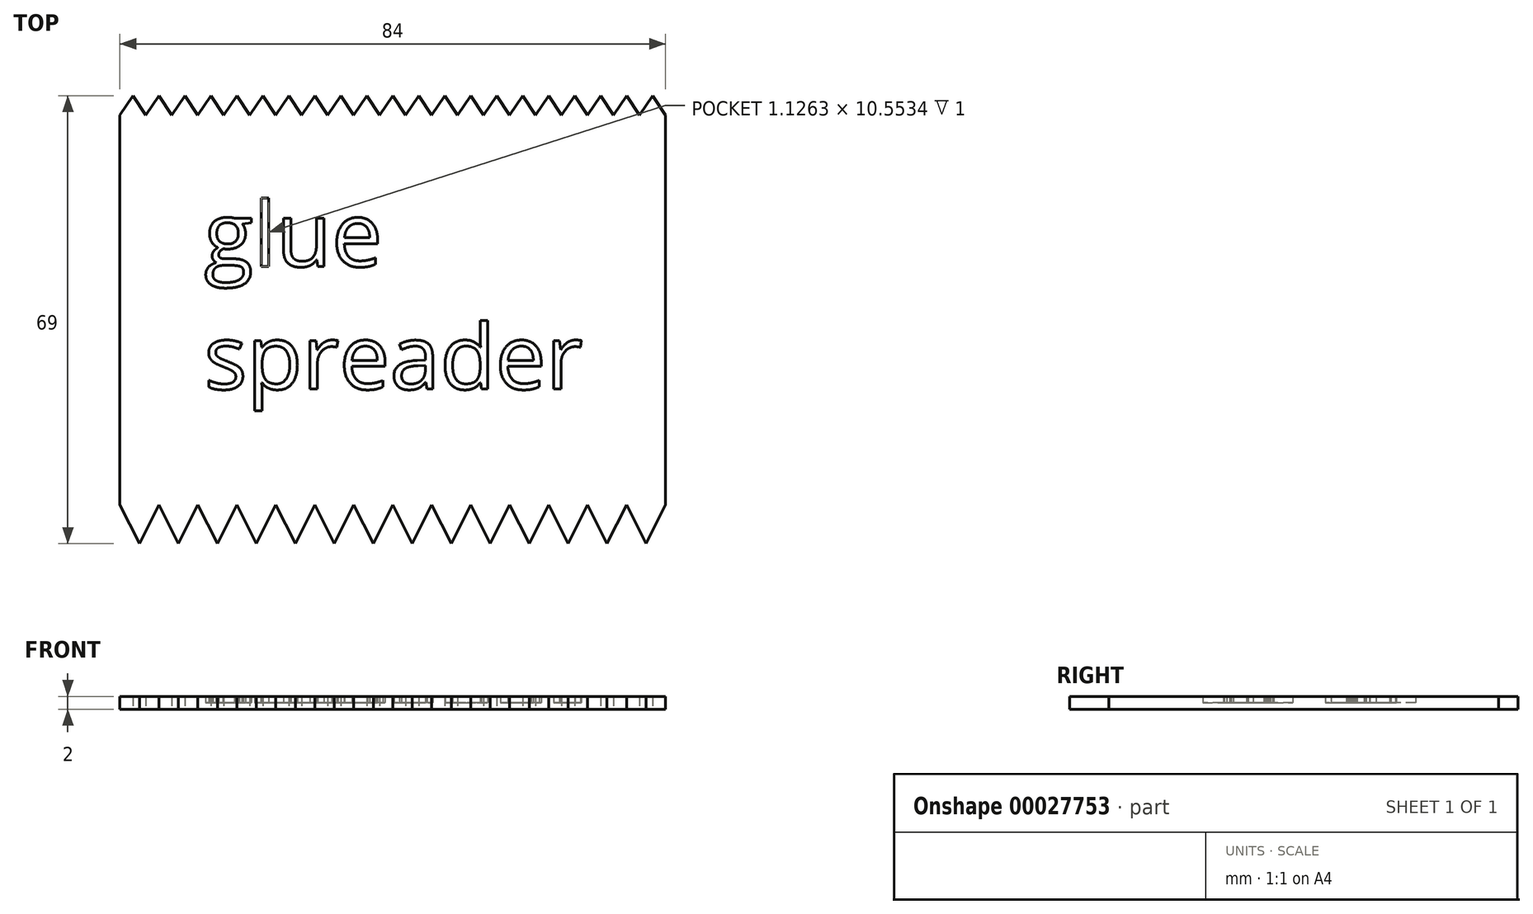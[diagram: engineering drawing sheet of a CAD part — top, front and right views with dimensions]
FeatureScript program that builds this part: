
annotation { "Feature Type Name" : "Feature", "Feature Type Description" : "" }
export const myFeature = defineFeature(function(context is Context, id is Id, definition is map)
    precondition{}
    {
        {
            var Q0;
            Q0=qCreatedBy(makeId("Top.planeOp"),FACE);
            var sketch = newSketch(context, id + "F0", { "sketchPlane" : qUnion([Q0])});
            skLineSegment(sketch, "E0.rect.bottom", {"start": v(42, 30) * mm, "end": v(-42, 30) * mm});
            skLineSegment(sketch, "E0.rect.top", {"start": v(42, -30) * mm, "end": v(-42, -30) * mm});
            skLineSegment(sketch, "E0.rect.left", {"start": v(42, 30) * mm, "end": v(42, -30) * mm});
            skLineSegment(sketch, "E0.rect.right", {"start": v(-42, 30) * mm, "end": v(-42, -30) * mm});
            skPoint(sketch, "E0.rect.middle", {"position": v(0, 0) * mm});
            skLineSegment(sketch, "E1", {"start": v(-42, 30) * mm, "end": v(-40, 33) * mm});
            skLineSegment(sketch, "E2", {"start": v(-40, 33) * mm, "end": v(-38, 30) * mm});
            skLineSegment(sketch, "E3.1.0.0", {"start": v(-38, 30) * mm, "end": v(-36, 33) * mm});
            skLineSegment(sketch, "E3.1.0.1", {"start": v(-36, 33) * mm, "end": v(-34, 30) * mm});
            skLineSegment(sketch, "E3.2.0.0", {"start": v(-34, 30) * mm, "end": v(-32, 33) * mm});
            skLineSegment(sketch, "E3.2.0.1", {"start": v(-32, 33) * mm, "end": v(-30, 30) * mm});
            skLineSegment(sketch, "E3.3.0.0", {"start": v(-30, 30) * mm, "end": v(-28, 33) * mm});
            skLineSegment(sketch, "E3.3.0.1", {"start": v(-28, 33) * mm, "end": v(-26, 30) * mm});
            skLineSegment(sketch, "E3.4.0.0", {"start": v(-26, 30) * mm, "end": v(-24, 33) * mm});
            skLineSegment(sketch, "E3.4.0.1", {"start": v(-24, 33) * mm, "end": v(-22, 30) * mm});
            skLineSegment(sketch, "E3.5.0.0", {"start": v(-22, 30) * mm, "end": v(-20, 33) * mm});
            skLineSegment(sketch, "E3.5.0.1", {"start": v(-20, 33) * mm, "end": v(-18, 30) * mm});
            skLineSegment(sketch, "E3.6.0.0", {"start": v(-18, 30) * mm, "end": v(-16, 33) * mm});
            skLineSegment(sketch, "E3.6.0.1", {"start": v(-16, 33) * mm, "end": v(-14, 30) * mm});
            skLineSegment(sketch, "E3.7.0.0", {"start": v(-14, 30) * mm, "end": v(-12, 33) * mm});
            skLineSegment(sketch, "E3.7.0.1", {"start": v(-12, 33) * mm, "end": v(-10, 30) * mm});
            skLineSegment(sketch, "E3.8.0.0", {"start": v(-10, 30) * mm, "end": v(-8, 33) * mm});
            skLineSegment(sketch, "E3.8.0.1", {"start": v(-8, 33) * mm, "end": v(-6, 30) * mm});
            skLineSegment(sketch, "E3.9.0.0", {"start": v(-6, 30) * mm, "end": v(-4, 33) * mm});
            skLineSegment(sketch, "E3.9.0.1", {"start": v(-4, 33) * mm, "end": v(-2, 30) * mm});
            skLineSegment(sketch, "E3.10.0.0", {"start": v(-2, 30) * mm, "end": v(0, 33) * mm});
            skLineSegment(sketch, "E3.10.0.1", {"start": v(0, 33) * mm, "end": v(2, 30) * mm});
            skLineSegment(sketch, "E3.11.0.0", {"start": v(2, 30) * mm, "end": v(4, 33) * mm});
            skLineSegment(sketch, "E3.11.0.1", {"start": v(4, 33) * mm, "end": v(6, 30) * mm});
            skLineSegment(sketch, "E3.12.0.0", {"start": v(6, 30) * mm, "end": v(8, 33) * mm});
            skLineSegment(sketch, "E3.12.0.1", {"start": v(8, 33) * mm, "end": v(10, 30) * mm});
            skLineSegment(sketch, "E3.13.0.0", {"start": v(10, 30) * mm, "end": v(12, 33) * mm});
            skLineSegment(sketch, "E3.13.0.1", {"start": v(12, 33) * mm, "end": v(14, 30) * mm});
            skLineSegment(sketch, "E3.14.0.0", {"start": v(14, 30) * mm, "end": v(16, 33) * mm});
            skLineSegment(sketch, "E3.14.0.1", {"start": v(16, 33) * mm, "end": v(18, 30) * mm});
            skLineSegment(sketch, "E3.direction1", {"start": v(-42, 30) * mm, "end": v(-38, 30) * mm, "construction": true});
            skLineSegment(sketch, "E4", {"start": v(-42, -30) * mm, "end": v(-39, -36) * mm});
            skLineSegment(sketch, "E5", {"start": v(-39, -36) * mm, "end": v(-36, -30) * mm});
            skLineSegment(sketch, "E6.1.0.0", {"start": v(-33, -36) * mm, "end": v(-30, -30) * mm});
            skLineSegment(sketch, "E6.1.0.1", {"start": v(-36, -30) * mm, "end": v(-33, -36) * mm});
            skLineSegment(sketch, "E6.2.0.0", {"start": v(-27, -36) * mm, "end": v(-24, -30) * mm});
            skLineSegment(sketch, "E6.2.0.1", {"start": v(-30, -30) * mm, "end": v(-27, -36) * mm});
            skLineSegment(sketch, "E6.3.0.0", {"start": v(-21, -36) * mm, "end": v(-18, -30) * mm});
            skLineSegment(sketch, "E6.3.0.1", {"start": v(-24, -30) * mm, "end": v(-21, -36) * mm});
            skLineSegment(sketch, "E6.4.0.0", {"start": v(-15, -36) * mm, "end": v(-12, -30) * mm});
            skLineSegment(sketch, "E6.4.0.1", {"start": v(-18, -30) * mm, "end": v(-15, -36) * mm});
            skLineSegment(sketch, "E6.5.0.0", {"start": v(-9, -36) * mm, "end": v(-6, -30) * mm});
            skLineSegment(sketch, "E6.5.0.1", {"start": v(-12, -30) * mm, "end": v(-9, -36) * mm});
            skLineSegment(sketch, "E6.6.0.0", {"start": v(-3, -36) * mm, "end": v(0, -30) * mm});
            skLineSegment(sketch, "E6.6.0.1", {"start": v(-6, -30) * mm, "end": v(-3, -36) * mm});
            skLineSegment(sketch, "E6.7.0.0", {"start": v(3, -36) * mm, "end": v(6, -30) * mm});
            skLineSegment(sketch, "E6.7.0.1", {"start": v(0, -30) * mm, "end": v(3, -36) * mm});
            skLineSegment(sketch, "E6.8.0.0", {"start": v(9, -36) * mm, "end": v(12, -30) * mm});
            skLineSegment(sketch, "E6.8.0.1", {"start": v(6, -30) * mm, "end": v(9, -36) * mm});
            skLineSegment(sketch, "E6.9.0.0", {"start": v(15, -36) * mm, "end": v(18, -30) * mm});
            skLineSegment(sketch, "E6.9.0.1", {"start": v(12, -30) * mm, "end": v(15, -36) * mm});
            skLineSegment(sketch, "E6.direction1", {"start": v(-39, -36) * mm, "end": v(-33, -36) * mm, "construction": true});
            skLineSegment(sketch, "E7.0.15.0", {"start": v(18, 30) * mm, "end": v(20, 33) * mm});
            skLineSegment(sketch, "E7.3.15.0", {"start": v(20, 33) * mm, "end": v(22, 30) * mm});
            skLineSegment(sketch, "E7.0.16.0", {"start": v(22, 30) * mm, "end": v(24, 33) * mm});
            skLineSegment(sketch, "E7.3.16.0", {"start": v(24, 33) * mm, "end": v(26, 30) * mm});
            skLineSegment(sketch, "E7.0.17.0", {"start": v(26, 30) * mm, "end": v(28, 33) * mm});
            skLineSegment(sketch, "E7.3.17.0", {"start": v(28, 33) * mm, "end": v(30, 30) * mm});
            skLineSegment(sketch, "E7.0.18.0", {"start": v(30, 30) * mm, "end": v(32, 33) * mm});
            skLineSegment(sketch, "E7.3.18.0", {"start": v(32, 33) * mm, "end": v(34, 30) * mm});
            skLineSegment(sketch, "E7.0.19.0", {"start": v(34, 30) * mm, "end": v(36, 33) * mm});
            skLineSegment(sketch, "E7.3.19.0", {"start": v(36, 33) * mm, "end": v(38, 30) * mm});
            skLineSegment(sketch, "E7.0.20.0", {"start": v(38, 30) * mm, "end": v(40, 33) * mm});
            skLineSegment(sketch, "E7.3.20.0", {"start": v(40, 33) * mm, "end": v(42, 30) * mm});
            skLineSegment(sketch, "E8.0.10.0", {"start": v(21, -36) * mm, "end": v(24, -30) * mm});
            skLineSegment(sketch, "E8.3.10.0", {"start": v(18, -30) * mm, "end": v(21, -36) * mm});
            skLineSegment(sketch, "E8.0.11.0", {"start": v(27, -36) * mm, "end": v(30, -30) * mm});
            skLineSegment(sketch, "E8.3.11.0", {"start": v(24, -30) * mm, "end": v(27, -36) * mm});
            skLineSegment(sketch, "E8.0.12.0", {"start": v(33, -36) * mm, "end": v(36, -30) * mm});
            skLineSegment(sketch, "E8.3.12.0", {"start": v(30, -30) * mm, "end": v(33, -36) * mm});
            skLineSegment(sketch, "E8.0.13.0", {"start": v(39, -36) * mm, "end": v(42, -30) * mm});
            skLineSegment(sketch, "E8.3.13.0", {"start": v(36, -30) * mm, "end": v(39, -36) * mm});
            skText(sketch, "E9", { "text": "glue\nspreader", "fontName": "OpenSans-Regular.ttf"});
            skLineSegment(sketch, "E10", {"start": v(0, 30) * mm, "end": v(0, -30) * mm, "construction": true});
            skLineSegment(sketch, "E11", {"start": v(-42, 0) * mm, "end": v(42, 0) * mm, "construction": true});
            const initialGuessF0  = {"E9": [-0.02905, 0.0067, 1, 0, 0.01]};
            skSetInitialGuess(sketch, initialGuessF0);
            skSolve(sketch);
        }
        {
            var Q0;
            {var subQ1=sQuery(id+"F0.wireOp",EDGE,"E7.0.18.0");Q0=makeQuery(id+"F0.imprint","IMPRINT",FACE,{"disambiguationData":[TD([[makeQuery(id+"F0.imprint","IMPRINT",EDGE,{"derivedFrom":subQ1}),-1.0]])]});}
            var Q1;
            {var subQ1=sQuery(id+"F0.wireOp",EDGE,"E3.8.0.0");Q1=makeQuery(id+"F0.imprint","IMPRINT",FACE,{"disambiguationData":[TD([[makeQuery(id+"F0.imprint","IMPRINT",EDGE,{"derivedFrom":subQ1}),-1.0]])]});}
            var Q2;
            {var subQ1=sQuery(id+"F0.wireOp",EDGE,"E3.10.0.0");Q2=makeQuery(id+"F0.imprint","IMPRINT",FACE,{"disambiguationData":[TD([[makeQuery(id+"F0.imprint","IMPRINT",EDGE,{"derivedFrom":subQ1}),-1.0]])]});}
            var Q3;
            {var subQ1=sQuery(id+"F0.wireOp",EDGE,"E7.0.19.0");Q3=makeQuery(id+"F0.imprint","IMPRINT",FACE,{"disambiguationData":[TD([[makeQuery(id+"F0.imprint","IMPRINT",EDGE,{"derivedFrom":subQ1}),-1.0]])]});}
            var Q4;
            {var subQ1=sQuery(id+"F0.wireOp",EDGE,"E3.13.0.0");Q4=makeQuery(id+"F0.imprint","IMPRINT",FACE,{"disambiguationData":[TD([[makeQuery(id+"F0.imprint","IMPRINT",EDGE,{"derivedFrom":subQ1}),-1.0]])]});}
            var Q5;
            {var subQ1=sQuery(id+"F0.wireOp",EDGE,"E7.0.17.0");Q5=makeQuery(id+"F0.imprint","IMPRINT",FACE,{"disambiguationData":[TD([[makeQuery(id+"F0.imprint","IMPRINT",EDGE,{"derivedFrom":subQ1}),-1.0]])]});}
            var Q6;
            {var subQ1=sQuery(id+"F0.wireOp",EDGE,"E7.0.16.0");Q6=makeQuery(id+"F0.imprint","IMPRINT",FACE,{"disambiguationData":[TD([[makeQuery(id+"F0.imprint","IMPRINT",EDGE,{"derivedFrom":subQ1}),-1.0]])]});}
            var Q7;
            {var subQ1=sQuery(id+"F0.wireOp",EDGE,"E7.0.15.0");Q7=makeQuery(id+"F0.imprint","IMPRINT",FACE,{"disambiguationData":[TD([[makeQuery(id+"F0.imprint","IMPRINT",EDGE,{"derivedFrom":subQ1}),-1.0]])]});}
            var Q8;
            {var subQ1=sQuery(id+"F0.wireOp",EDGE,"E6.6.0.0");Q8=makeQuery(id+"F0.imprint","IMPRINT",FACE,{"disambiguationData":[TD([[makeQuery(id+"F0.imprint","IMPRINT",EDGE,{"derivedFrom":subQ1}),1.0]])]});}
            var Q9;
            {var subQ1=sQuery(id+"F0.wireOp",EDGE,"E8.0.13.0");Q9=makeQuery(id+"F0.imprint","IMPRINT",FACE,{"disambiguationData":[TD([[makeQuery(id+"F0.imprint","IMPRINT",EDGE,{"derivedFrom":subQ1}),1.0]])]});}
            var Q10;
            {var subQ1=sQuery(id+"F0.wireOp",EDGE,"E6.4.0.0");Q10=makeQuery(id+"F0.imprint","IMPRINT",FACE,{"disambiguationData":[TD([[makeQuery(id+"F0.imprint","IMPRINT",EDGE,{"derivedFrom":subQ1}),1.0]])]});}
            var Q11;
            {var subQ1=sQuery(id+"F0.wireOp",EDGE,"E6.5.0.0");Q11=makeQuery(id+"F0.imprint","IMPRINT",FACE,{"disambiguationData":[TD([[makeQuery(id+"F0.imprint","IMPRINT",EDGE,{"derivedFrom":subQ1}),1.0]])]});}
            var Q12;
            {var subQ1=sQuery(id+"F0.wireOp",EDGE,"E8.0.11.0");Q12=makeQuery(id+"F0.imprint","IMPRINT",FACE,{"disambiguationData":[TD([[makeQuery(id+"F0.imprint","IMPRINT",EDGE,{"derivedFrom":subQ1}),1.0]])]});}
            var Q13;
            {var subQ1=sQuery(id+"F0.wireOp",EDGE,"E3.3.0.0");Q13=makeQuery(id+"F0.imprint","IMPRINT",FACE,{"disambiguationData":[TD([[makeQuery(id+"F0.imprint","IMPRINT",EDGE,{"derivedFrom":subQ1}),-1.0]])]});}
            var Q14;
            {var subQ1=sQuery(id+"F0.wireOp",EDGE,"E6.1.0.0");Q14=makeQuery(id+"F0.imprint","IMPRINT",FACE,{"disambiguationData":[TD([[makeQuery(id+"F0.imprint","IMPRINT",EDGE,{"derivedFrom":subQ1}),1.0]])]});}
            var Q15;
            {var subQ1=sQuery(id+"F0.wireOp",EDGE,"E8.0.12.0");Q15=makeQuery(id+"F0.imprint","IMPRINT",FACE,{"disambiguationData":[TD([[makeQuery(id+"F0.imprint","IMPRINT",EDGE,{"derivedFrom":subQ1}),1.0]])]});}
            var Q16;
            {var subQ1=sQuery(id+"F0.wireOp",EDGE,"E3.5.0.0");Q16=makeQuery(id+"F0.imprint","IMPRINT",FACE,{"disambiguationData":[TD([[makeQuery(id+"F0.imprint","IMPRINT",EDGE,{"derivedFrom":subQ1}),-1.0]])]});}
            var Q17;
            {var subQ1=sQuery(id+"F0.wireOp",EDGE,"E3.7.0.0");Q17=makeQuery(id+"F0.imprint","IMPRINT",FACE,{"disambiguationData":[TD([[makeQuery(id+"F0.imprint","IMPRINT",EDGE,{"derivedFrom":subQ1}),-1.0]])]});}
            var Q18;
            {var subQ1=sQuery(id+"F0.wireOp",EDGE,"E6.7.0.0");Q18=makeQuery(id+"F0.imprint","IMPRINT",FACE,{"disambiguationData":[TD([[makeQuery(id+"F0.imprint","IMPRINT",EDGE,{"derivedFrom":subQ1}),1.0]])]});}
            var Q19;
            {var subQ1=sQuery(id+"F0.wireOp",EDGE,"E6.2.0.0");Q19=makeQuery(id+"F0.imprint","IMPRINT",FACE,{"disambiguationData":[TD([[makeQuery(id+"F0.imprint","IMPRINT",EDGE,{"derivedFrom":subQ1}),1.0]])]});}
            var Q20;
            {var subQ1=sQuery(id+"F0.wireOp",EDGE,"E7.0.20.0");Q20=makeQuery(id+"F0.imprint","IMPRINT",FACE,{"disambiguationData":[TD([[makeQuery(id+"F0.imprint","IMPRINT",EDGE,{"derivedFrom":subQ1}),-1.0]])]});}
            var Q21;
            {var subQ1=sQuery(id+"F0.wireOp",EDGE,"E1");Q21=makeQuery(id+"F0.imprint","IMPRINT",FACE,{"disambiguationData":[TD([[makeQuery(id+"F0.imprint","IMPRINT",EDGE,{"derivedFrom":subQ1}),-1.0]])]});}
            var Q22;
            {var subQ1=sQuery(id+"F0.wireOp",EDGE,"E3.9.0.0");Q22=makeQuery(id+"F0.imprint","IMPRINT",FACE,{"disambiguationData":[TD([[makeQuery(id+"F0.imprint","IMPRINT",EDGE,{"derivedFrom":subQ1}),-1.0]])]});}
            var Q23;
            {var subQ1=sQuery(id+"F0.wireOp",EDGE,"E3.11.0.0");Q23=makeQuery(id+"F0.imprint","IMPRINT",FACE,{"disambiguationData":[TD([[makeQuery(id+"F0.imprint","IMPRINT",EDGE,{"derivedFrom":subQ1}),-1.0]])]});}
            var Q24;
            {var subQ1=sQuery(id+"F0.wireOp",EDGE,"E3.12.0.0");Q24=makeQuery(id+"F0.imprint","IMPRINT",FACE,{"disambiguationData":[TD([[makeQuery(id+"F0.imprint","IMPRINT",EDGE,{"derivedFrom":subQ1}),-1.0]])]});}
            var Q25;
            {var subQ1=sQuery(id+"F0.wireOp",EDGE,"E3.6.0.0");Q25=makeQuery(id+"F0.imprint","IMPRINT",FACE,{"disambiguationData":[TD([[makeQuery(id+"F0.imprint","IMPRINT",EDGE,{"derivedFrom":subQ1}),-1.0]])]});}
            var Q26;
            {var subQ1=sQuery(id+"F0.wireOp",EDGE,"E8.0.10.0");Q26=makeQuery(id+"F0.imprint","IMPRINT",FACE,{"disambiguationData":[TD([[makeQuery(id+"F0.imprint","IMPRINT",EDGE,{"derivedFrom":subQ1}),1.0]])]});}
            var Q27;
            {var subQ1=sQuery(id+"F0.wireOp",EDGE,"E3.4.0.0");Q27=makeQuery(id+"F0.imprint","IMPRINT",FACE,{"disambiguationData":[TD([[makeQuery(id+"F0.imprint","IMPRINT",EDGE,{"derivedFrom":subQ1}),-1.0]])]});}
            var Q28;
            {var subQ1=sQuery(id+"F0.wireOp",EDGE,"E3.14.0.0");Q28=makeQuery(id+"F0.imprint","IMPRINT",FACE,{"disambiguationData":[TD([[makeQuery(id+"F0.imprint","IMPRINT",EDGE,{"derivedFrom":subQ1}),-1.0]])]});}
            var Q29;
            {var subQ1=sQuery(id+"F0.wireOp",EDGE,"E3.2.0.0");Q29=makeQuery(id+"F0.imprint","IMPRINT",FACE,{"disambiguationData":[TD([[makeQuery(id+"F0.imprint","IMPRINT",EDGE,{"derivedFrom":subQ1}),-1.0]])]});}
            var Q30;
            {var subQ0=sQuery(id+"F0.wireOp",EDGE,"E4");Q30=makeQuery(id+"F0.imprint","IMPRINT",FACE,{"disambiguationData":[TD([[makeQuery(id+"F0.imprint","IMPRINT",EDGE,{"derivedFrom":subQ0}),1.0]])]});}
            var Q31;
            {var subQ1=sQuery(id+"F0.wireOp",EDGE,"E6.3.0.0");Q31=makeQuery(id+"F0.imprint","IMPRINT",FACE,{"disambiguationData":[TD([[makeQuery(id+"F0.imprint","IMPRINT",EDGE,{"derivedFrom":subQ1}),1.0]])]});}
            var Q32;
            {var subQ1=sQuery(id+"F0.wireOp",EDGE,"E6.9.0.0");Q32=makeQuery(id+"F0.imprint","IMPRINT",FACE,{"disambiguationData":[TD([[makeQuery(id+"F0.imprint","IMPRINT",EDGE,{"derivedFrom":subQ1}),1.0]])]});}
            var Q33;
            {var subQ1=sQuery(id+"F0.wireOp",EDGE,"E6.8.0.0");Q33=makeQuery(id+"F0.imprint","IMPRINT",FACE,{"disambiguationData":[TD([[makeQuery(id+"F0.imprint","IMPRINT",EDGE,{"derivedFrom":subQ1}),1.0]])]});}
            var Q34;
            {var subQ1=sQuery(id+"F0.wireOp",EDGE,"E0.rect.left");Q34=makeQuery(id+"F0.imprint","IMPRINT",FACE,{"disambiguationData":[TD([[makeQuery(id+"F0.imprint","IMPRINT",EDGE,{"derivedFrom":subQ1}),-1.0]])]});}
            var Q35;
            {var subQ1=sQuery(id+"F0.wireOp",EDGE,"E3.1.0.0");Q35=makeQuery(id+"F0.imprint","IMPRINT",FACE,{"disambiguationData":[TD([[makeQuery(id+"F0.imprint","IMPRINT",EDGE,{"derivedFrom":subQ1}),-1.0]])]});}
            var Q36;
            Q36=makeQuery(id+"F0.imprint","IMPRINT",FACE,{"disambiguationData":[TD([[makeQuery(id+"F0.imprint","IMPRINT",EDGE,{"derivedFrom":sQuery(id+"F0.wireOp",EDGE,"E9.sketch_text.stroke-38")}),1.0]])]});
            var Q37;
            Q37=makeQuery(id+"F0.imprint","IMPRINT",FACE,{"disambiguationData":[TD([[makeQuery(id+"F0.imprint","IMPRINT",EDGE,{"derivedFrom":sQuery(id+"F0.wireOp",EDGE,"E9.sketch_text.stroke-29")}),1.0]])]});
            var Q38;
            Q38=makeQuery(id+"F0.imprint","IMPRINT",FACE,{"disambiguationData":[TD([[makeQuery(id+"F0.imprint","IMPRINT",EDGE,{"derivedFrom":sQuery(id+"F0.wireOp",EDGE,"E9.sketch_text.stroke-79")}),1.0]])]});
            var Q39;
            Q39=makeQuery(id+"F0.imprint","IMPRINT",FACE,{"disambiguationData":[TD([[makeQuery(id+"F0.imprint","IMPRINT",EDGE,{"derivedFrom":sQuery(id+"F0.wireOp",EDGE,"E9.sketch_text.stroke-125")}),1.0]])]});
            var Q40;
            Q40=makeQuery(id+"F0.imprint","IMPRINT",FACE,{"disambiguationData":[TD([[makeQuery(id+"F0.imprint","IMPRINT",EDGE,{"derivedFrom":sQuery(id+"F0.wireOp",EDGE,"E9.sketch_text.stroke-161")}),1.0]])]});
            var Q41;
            Q41=makeQuery(id+"F0.imprint","IMPRINT",FACE,{"disambiguationData":[TD([[makeQuery(id+"F0.imprint","IMPRINT",EDGE,{"derivedFrom":sQuery(id+"F0.wireOp",EDGE,"E9.sketch_text.stroke-185")}),1.0]])]});
            var Q42;
            Q42=makeQuery(id+"F0.imprint","IMPRINT",FACE,{"disambiguationData":[TD([[makeQuery(id+"F0.imprint","IMPRINT",EDGE,{"derivedFrom":sQuery(id+"F0.wireOp",EDGE,"E9.sketch_text.stroke-208")}),1.0]])]});
            var Q43;
            Q43=makeQuery(id+"F0.imprint","IMPRINT",FACE,{"disambiguationData":[TD([[makeQuery(id+"F0.imprint","IMPRINT",EDGE,{"derivedFrom":sQuery(id+"F0.wireOp",EDGE,"E9.sketch_text.stroke-231")}),1.0]])]});
            extrude(context, id + "F1", {"entities" : qUnion([Q0, Q1, Q2, Q3, Q4, Q5, Q6, Q7, Q8, Q9, Q10, Q11, Q12, Q13, Q14, Q15, Q16, Q17, Q18, Q19, Q20, Q21, Q22, Q23, Q24, Q25, Q26, Q27, Q28, Q29, Q30, Q31, Q32, Q33, Q34, Q35, Q36, Q37, Q38, Q39, Q40, Q41, Q42, Q43]), "depth" : 2 * mm});
        }
        {
            var Q0;
            Q0=makeQuery(id+"F0.imprint","IMPRINT",FACE,{"disambiguationData":[TD([[makeQuery(id+"F0.imprint","IMPRINT",EDGE,{"derivedFrom":sQuery(id+"F0.wireOp",EDGE,"E9.sketch_text.stroke-0")}),-1.0]])]});
            var Q1;
            Q1=makeQuery(id+"F0.imprint","IMPRINT",FACE,{"disambiguationData":[TD([[makeQuery(id+"F0.imprint","IMPRINT",EDGE,{"derivedFrom":sQuery(id+"F0.wireOp",EDGE,"E9.sketch_text.stroke-44")}),-1.0]])]});
            var Q2;
            Q2=makeQuery(id+"F0.imprint","IMPRINT",FACE,{"disambiguationData":[TD([[makeQuery(id+"F0.imprint","IMPRINT",EDGE,{"derivedFrom":sQuery(id+"F0.wireOp",EDGE,"E9.sketch_text.stroke-48")}),-1.0]])]});
            var Q3;
            Q3=makeQuery(id+"F0.imprint","IMPRINT",FACE,{"disambiguationData":[TD([[makeQuery(id+"F0.imprint","IMPRINT",EDGE,{"derivedFrom":sQuery(id+"F0.wireOp",EDGE,"E9.sketch_text.stroke-65")}),-1.0]])]});
            var Q4;
            Q4=makeQuery(id+"F0.imprint","IMPRINT",FACE,{"disambiguationData":[TD([[makeQuery(id+"F0.imprint","IMPRINT",EDGE,{"derivedFrom":sQuery(id+"F0.wireOp",EDGE,"E9.sketch_text.stroke-84")}),-1.0]])]});
            var Q5;
            Q5=makeQuery(id+"F0.imprint","IMPRINT",FACE,{"disambiguationData":[TD([[makeQuery(id+"F0.imprint","IMPRINT",EDGE,{"derivedFrom":sQuery(id+"F0.wireOp",EDGE,"E9.sketch_text.stroke-109")}),-1.0]])]});
            var Q6;
            Q6=makeQuery(id+"F0.imprint","IMPRINT",FACE,{"disambiguationData":[TD([[makeQuery(id+"F0.imprint","IMPRINT",EDGE,{"derivedFrom":sQuery(id+"F0.wireOp",EDGE,"E9.sketch_text.stroke-134")}),-1.0]])]});
            var Q7;
            Q7=makeQuery(id+"F0.imprint","IMPRINT",FACE,{"disambiguationData":[TD([[makeQuery(id+"F0.imprint","IMPRINT",EDGE,{"derivedFrom":sQuery(id+"F0.wireOp",EDGE,"E9.sketch_text.stroke-147")}),-1.0]])]});
            var Q8;
            Q8=makeQuery(id+"F0.imprint","IMPRINT",FACE,{"disambiguationData":[TD([[makeQuery(id+"F0.imprint","IMPRINT",EDGE,{"derivedFrom":sQuery(id+"F0.wireOp",EDGE,"E9.sketch_text.stroke-166")}),-1.0]])]});
            var Q9;
            Q9=makeQuery(id+"F0.imprint","IMPRINT",FACE,{"disambiguationData":[TD([[makeQuery(id+"F0.imprint","IMPRINT",EDGE,{"derivedFrom":sQuery(id+"F0.wireOp",EDGE,"E9.sketch_text.stroke-193")}),-1.0]])]});
            var Q10;
            Q10=makeQuery(id+"F0.imprint","IMPRINT",FACE,{"disambiguationData":[TD([[makeQuery(id+"F0.imprint","IMPRINT",EDGE,{"derivedFrom":sQuery(id+"F0.wireOp",EDGE,"E9.sketch_text.stroke-217")}),-1.0]])]});
            var Q11;
            Q11=makeQuery(id+"F0.imprint","IMPRINT",FACE,{"disambiguationData":[TD([[makeQuery(id+"F0.imprint","IMPRINT",EDGE,{"derivedFrom":sQuery(id+"F0.wireOp",EDGE,"E9.sketch_text.stroke-236")}),-1.0]])]});
            extrude(context, id + "F2", {"entities" : qUnion([Q0, Q1, Q2, Q3, Q4, Q5, Q6, Q7, Q8, Q9, Q10, Q11]), "operationType" : NewBodyOperationType.ADD, "depth" : 1 * mm});
        }
    });
